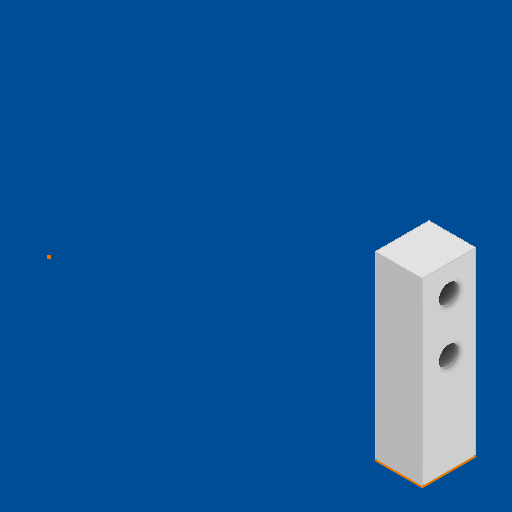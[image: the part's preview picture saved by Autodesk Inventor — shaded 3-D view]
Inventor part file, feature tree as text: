
AUTODESK INVENTOR PART (.ipt)
format: ipt  version: 2025 (Build 290162000, 162)  size: 180,736 bytes
history: native  units: in
note: dims shown in document units (in); Inventor stores cm internally (conversion verified against a paired STEP export)
features: direct_edit x6, other x6, move_body x5, hole x2, sketch x2, plane x1, split x1
ambient origin geometry x8: Origin, YZ Plane, XZ Plane, XY Plane, X Axis, Y Axis, Z Axis, Center Point
bodies: Solid1 (feature_tree), Body3 (feature_tree)
feature tree (23):
  move_body  "Move Body1"
  direct_edit  "Direct Edit1"
  direct_edit  "Direct Edit2"
  direct_edit  "Direct Edit3"
  hole  "Hole1"  [1 undecoded]
  direct_edit  "Direct Edit4"
  plane  "Work Plane1"
  split  "Split1"
  direct_edit  "Direct Edit5"
  sketch  "Sketch3"  dims[d2=0.0625in d3=0.0625in d4=0.1181in d5=0.0in d6=0.0089in d7=90.0deg d8=0.0968in d9=0.2362in d10=0.1575in d11=0.0787in d12=90.0deg d13=0.3465in d14=0.8108in d15=0.0039in d16=0.0039in d17=-0.315in d19=0.0in d20=0.0in d21=0.4154in d42=0.3937in d43=0.3937in d32=0.1936in d33=0.3543in d34=0.1575in d35=0.0787in d36=90.0deg d37=0.3543in d38=0.8108in d47=0.0102in d48=0.0in d49=0.0in d50=0.0in d51=-0.0043in d52=0.0in d53=0.0in d54=-0.0043in d55=0.0in d22=0.0197in d23=0.0344in d24=0.0197in d25=0.0344in]
  other  "Work Point1"
  hole  "Hole3"  [1 undecoded]
  direct_edit  "Direct Edit8"
  sketch  "Sketch1"  dims[d0=45.0deg d1=0.0059in]
  other  "Size1"
  other  "Size2"
  other  "Size3"
  other  "Size4"
  other  "Size5"
  move_body  "Move1"
  move_body  "Move4"
  move_body  "Move5"
  move_body  "Move6"
note: 2 required parameter values undecoded (feature->parameter linkage not recoverable at this tier; creation-order binding heuristic only, values carry confidence <= 0.55)
